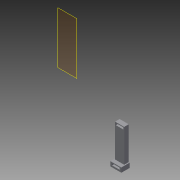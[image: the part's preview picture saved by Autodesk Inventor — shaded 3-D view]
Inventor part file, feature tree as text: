
AUTODESK INVENTOR PART (.ipt)
format: ipt  version: 2015 (Build 190159000, 159)  size: 204,800 bytes
history: native  units: in
note: dims shown in document units (in); Inventor stores cm internally (conversion verified against a paired STEP export)
features: extrude x7, sketch x7, projected_geometry x5, reference x2, plane x1, fillet x1
ambient origin geometry x8: Origin, YZ Plane, XZ Plane, XY Plane, X Axis, Y Axis, Z Axis, Center Point
bodies: Solid1 (feature_tree)
feature tree (23):
  plane  "Work Plane1"
  extrude  "Extrusion1"  Depth=0.1in TaperAngle=0.0deg
  extrude  "Extrusion2"  Depth=0.125in
  extrude  "Extrusion3"  Depth=0.125in
  extrude  "Extrusion4"  Depth=0.5in TaperAngle=0.0deg
  extrude  "Extrusion5"  Depth=0.75in
  extrude  "Extrusion6"  Depth=0.5in TaperAngle=0.0deg
  fillet  "Fillet1"  Radius=0.5in
  extrude  "Extrusion7"  Depth=0.125in
  sketch  "Sketch1"  dims[d2=0.5in d3=0.0in d4=0.1in d5=0.0in]
  reference  "Reference1"
  reference  "Reference2"
  sketch  "Sketch2"  dims[d6=0.125in d9=0.125in]
  sketch  "Sketch3"  dims[d10=0.125in d11=0.125in]
  projected_geometry  "Projected Loop1"
  sketch  "Sketch4"  dims[d12=0.625in d13=0.0in d14=0.5in d15=0.0in]
  projected_geometry  "Projected Loop2"
  sketch  "Sketch5"  dims[d16=0.75in d17=0.2in]
  projected_geometry  "Projected Loop3"
  sketch  "Sketch6"  dims[d18=0.2in d19=0.5in d20=0.0in d21=0.5in d22=0.0in]
  projected_geometry  "Projected Loop4"
  sketch  "Sketch7"  dims[d23=0.875in d24=0.125in d25=0.125in d26=0.5in d27=0.0in]
  projected_geometry  "Projected Loop5"
